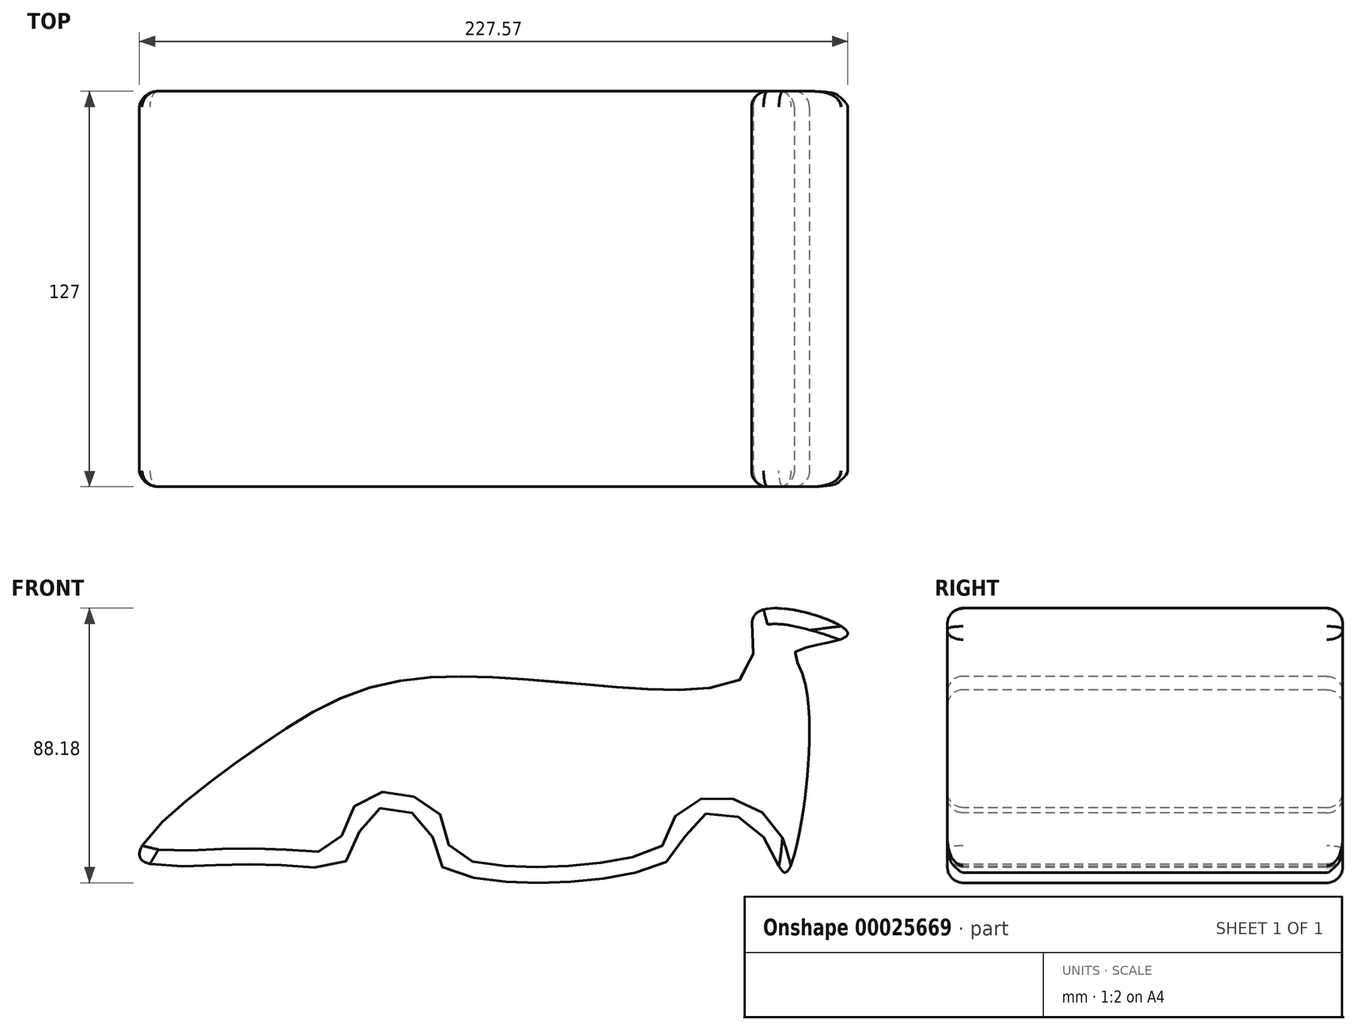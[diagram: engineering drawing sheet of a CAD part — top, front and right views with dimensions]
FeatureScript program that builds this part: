
annotation { "Feature Type Name" : "Feature", "Feature Type Description" : "" }
export const myFeature = defineFeature(function(context is Context, id is Id, definition is map)
    precondition{}
    {
        {
            var Q0;
            Q0=qCreatedBy(makeId("Front.planeOp"),FACE);
            var sketch = newSketch(context, id + "F0", { "sketchPlane" : qUnion([Q0])});
            skFitSpline(sketch, "E0", {"points": [v(-103.47, 0) * mm, v(-40.88, 21.86) * mm, v(53, 23.45) * mm, v(55.87, 42.61) * mm, v(84.61, 35.59) * mm, v(68.33, 30.16) * mm, v(70.88, 19.94) * mm, v(64.82, -41.05) * mm, v(54.92, -26.68) * mm, v(34.48, -24.45) * mm, v(28.1, -36.58) * mm, v(-46, -39.14) * mm, v(-49.82, -26.36) * mm, v(-68.35, -21.57) * mm, v(-75.7, -36.58) * mm, v(-104.43, -38.5) * mm, v(-142.8, -36.24) * mm, v(-103.47, 0) * mm]});
            skSolve(sketch);
        }
        {
            var Q0;
            Q0=makeQuery(id+"F0.imprint","IMPRINT",FACE,{"disambiguationData":[TD([[makeQuery(id+"F0.imprint","IMPRINT",EDGE,{"derivedFrom":sQuery(id+"F0.wireOp",EDGE,"E0")}),-1.0]])]});
            extrude(context, id + "F1", {"entities" : qUnion([Q0]), "depth" : 127 * mm});
        }
        {
            var Q0;
            Q0=makeQuery(id+"F1.opExtrude","CAP_EDGE",EDGE,{"disambiguationData":[OSD([sQuery(id+"F0.wireOp",EDGE,"E0")])],"isStart":false});
            var Q1;
            Q1=makeQuery(id+"F1.opExtrude","CAP_EDGE",EDGE,{"disambiguationData":[OSD([sQuery(id+"F0.wireOp",EDGE,"E0")])],"isStart":true});
            fillet(context, id + "F2", {"entities" : qUnion([Q0, Q1]), "radius" : 5.08 * mm, "tangentPropagation" : true, "allowEdgeOverflow" : false});
        }
    });
